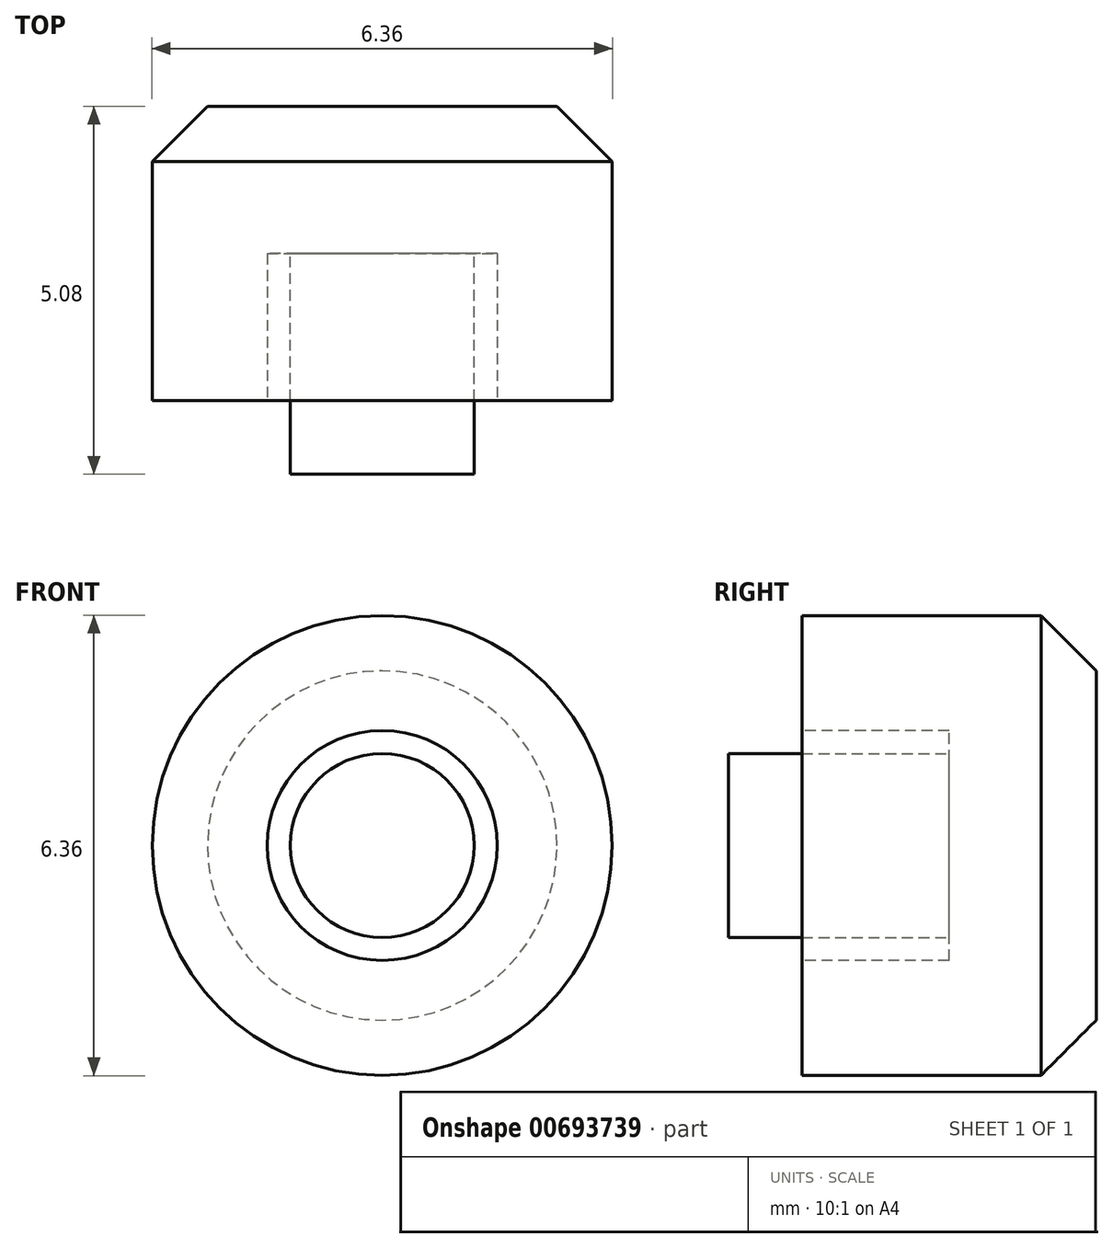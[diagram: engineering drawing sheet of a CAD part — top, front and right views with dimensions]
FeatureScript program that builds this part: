
annotation { "Feature Type Name" : "Feature", "Feature Type Description" : "" }
export const myFeature = defineFeature(function(context is Context, id is Id, definition is map)
    precondition{}
    {
        {
            var Q0;
            Q0=qCreatedBy(makeId("Front.planeOp"),FACE);
            var sketch = newSketch(context, id + "F0", { "sketchPlane" : qUnion([Q0])});
            skCircle(sketch, "E0", {"center": v(0, 0) * mm, "radius": 3.18 * mm});
            skSolve(sketch);
        }
        {
            var Q0;
            Q0 = qSketchRegion(id + "F0", true);
            extrude(context, id + "F1", {"entities" : qUnion([Q0]), "depth" : 4.06 * mm, "offsetDistance" : 25.4 * mm});
        }
        {
            var Q0;
            Q0=makeQuery(id+"F1.opExtrude","CAP_FACE",FACE,{"disambiguationData":[OSD([sQuery(id+"F0.wireOp",EDGE,"E0")])],"isStart":false});
            var sketch = newSketch(context, id + "F2", { "sketchPlane" : qUnion([Q0])});
            skCircle(sketch, "E1", {"center": v(0, 0) * mm, "radius": 1.59 * mm});
            skSolve(sketch);
        }
        {
            var Q0;
            Q0 = qSketchRegion(id + "F2", true);
            extrude(context, id + "F3", {"entities" : qUnion([Q0]), "operationType" : NewBodyOperationType.REMOVE, "oppositeDirection" : true, "depth" : 2.03 * mm, "offsetDistance" : 25.4 * mm});
        }
        {
            var Q0;
            Q0=makeQuery(id+"F3.boolean.opBoolean","COPY",FACE,{"derivedFrom":makeQuery(id+"F3.opExtrude","CAP_FACE",FACE,{"disambiguationData":[OSD([sQuery(id+"F2.wireOp",EDGE,"E1")])],"isStart":false})});
            var sketch = newSketch(context, id + "F4", { "sketchPlane" : qUnion([Q0])});
            skCircle(sketch, "E2", {"center": v(0, 0) * mm, "radius": 1.27 * mm});
            skSolve(sketch);
        }
        {
            var Q0;
            Q0 = qSketchRegion(id + "F4", true);
            extrude(context, id + "F5", {"entities" : qUnion([Q0]), "operationType" : NewBodyOperationType.ADD, "depth" : 3.05 * mm, "offsetDistance" : 25.4 * mm});
        }
        {
            var Q0;
            Q0=makeQuery(id+"F1.opExtrude","CAP_EDGE",EDGE,{"disambiguationData":[OSD([sQuery(id+"F0.wireOp",EDGE,"E0")])],"isStart":true});
            chamfer(context, id + "F6", {"entities" : qUnion([Q0]), "width" : 0.76 * mm, "tangentPropagation" : true});
        }
    });
